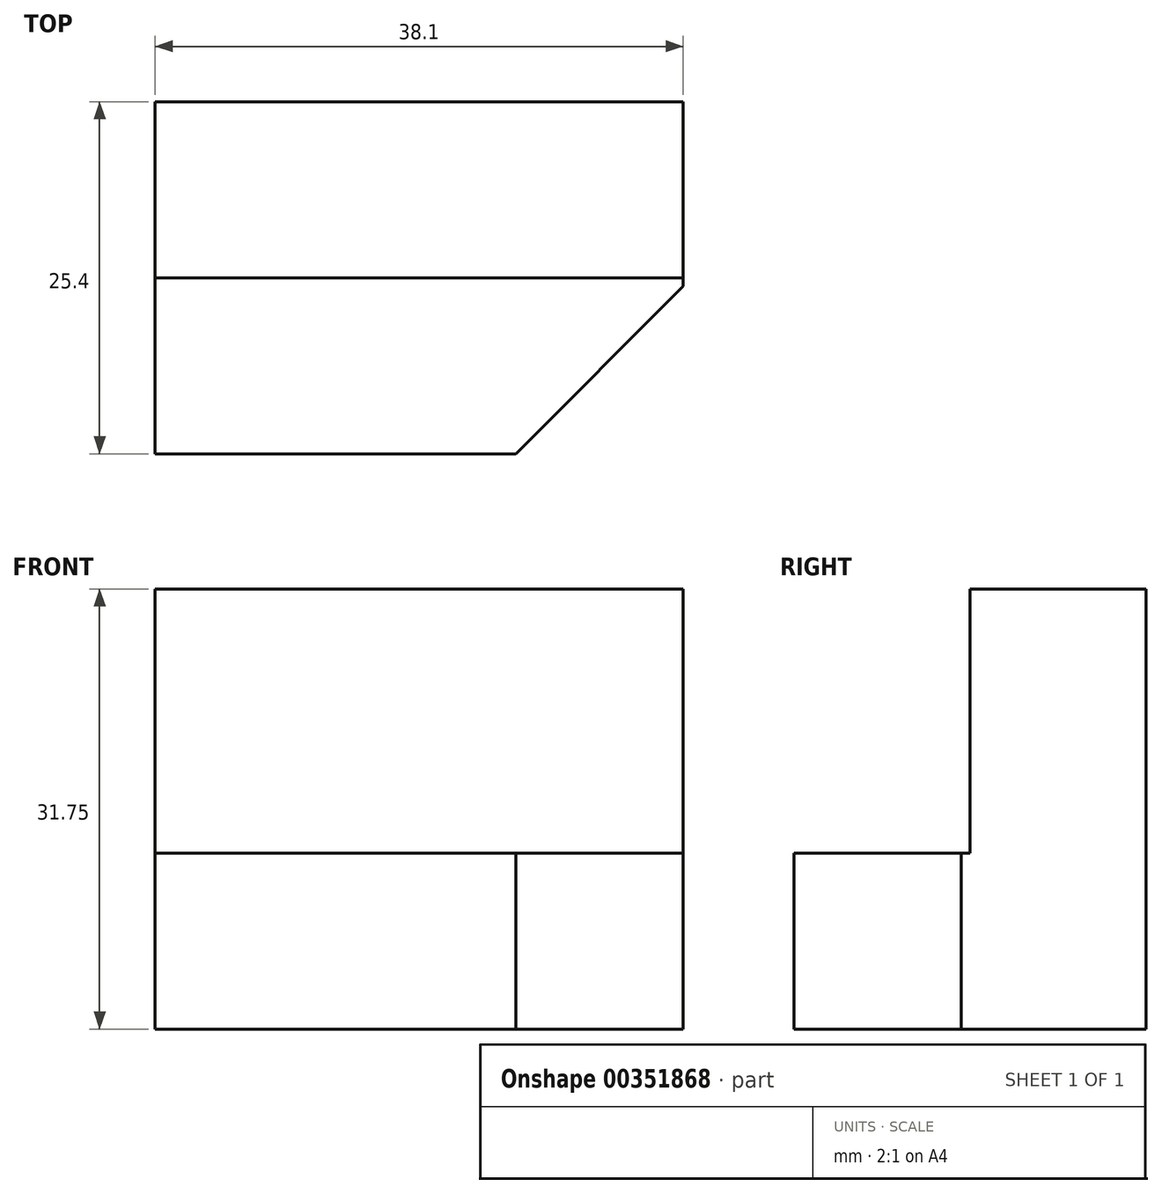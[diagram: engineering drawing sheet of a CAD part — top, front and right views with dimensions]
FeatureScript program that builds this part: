
annotation { "Feature Type Name" : "Feature", "Feature Type Description" : "" }
export const myFeature = defineFeature(function(context is Context, id is Id, definition is map)
    precondition{}
    {
        {
            var Q0;
            Q0=qCreatedBy(makeId("Right.planeOp"),FACE);
            var sketch = newSketch(context, id + "F0", { "sketchPlane" : qUnion([Q0])});
            skLineSegment(sketch, "E0", {"start": v(0, 0) * mm, "end": v(25.4, 0) * mm});
            skLineSegment(sketch, "E1", {"start": v(25.4, 0) * mm, "end": v(25.4, 31.75) * mm});
            skLineSegment(sketch, "E2", {"start": v(25.4, 31.75) * mm, "end": v(12.7, 31.75) * mm});
            skLineSegment(sketch, "E3", {"start": v(12.7, 31.75) * mm, "end": v(12.7, 12.7) * mm});
            skLineSegment(sketch, "E4", {"start": v(12.7, 12.7) * mm, "end": v(0, 12.7) * mm});
            skLineSegment(sketch, "E5", {"start": v(0, 12.7) * mm, "end": v(0, 0) * mm});
            skSolve(sketch);
        }
        {
            var Q0;
            Q0=makeQuery(id+"F0.imprint","IMPRINT",FACE,{"disambiguationData":[TD([[makeQuery(id+"F0.imprint","IMPRINT",EDGE,{"derivedFrom":sQuery(id+"F0.wireOp",EDGE,"E0")}),1.0]])]});
            extrude(context, id + "F1", {"entities" : qUnion([Q0]), "depth" : 38.1 * mm});
        }
        {
            var Q0;
            Q0=qCreatedBy(makeId("Top.planeOp"),FACE);
            var sketch = newSketch(context, id + "F2", { "sketchPlane" : qUnion([Q0])});
            skLineSegment(sketch, "E6", {"start": v(38.73, 0) * mm, "end": v(26.03, 0) * mm});
            skLineSegment(sketch, "E7", {"start": v(26.03, 0) * mm, "end": v(38.73, 12.7) * mm});
            skLineSegment(sketch, "E8", {"start": v(38.73, 12.7) * mm, "end": v(38.73, 0) * mm});
            skSolve(sketch);
        }
        {
            var Q0;
            Q0 = qSketchRegion(id + "F2", true);
            extrude(context, id + "F3", {"entities" : qUnion([Q0]), "operationType" : NewBodyOperationType.REMOVE, "depth" : 25.4 * mm});
        }
    });
